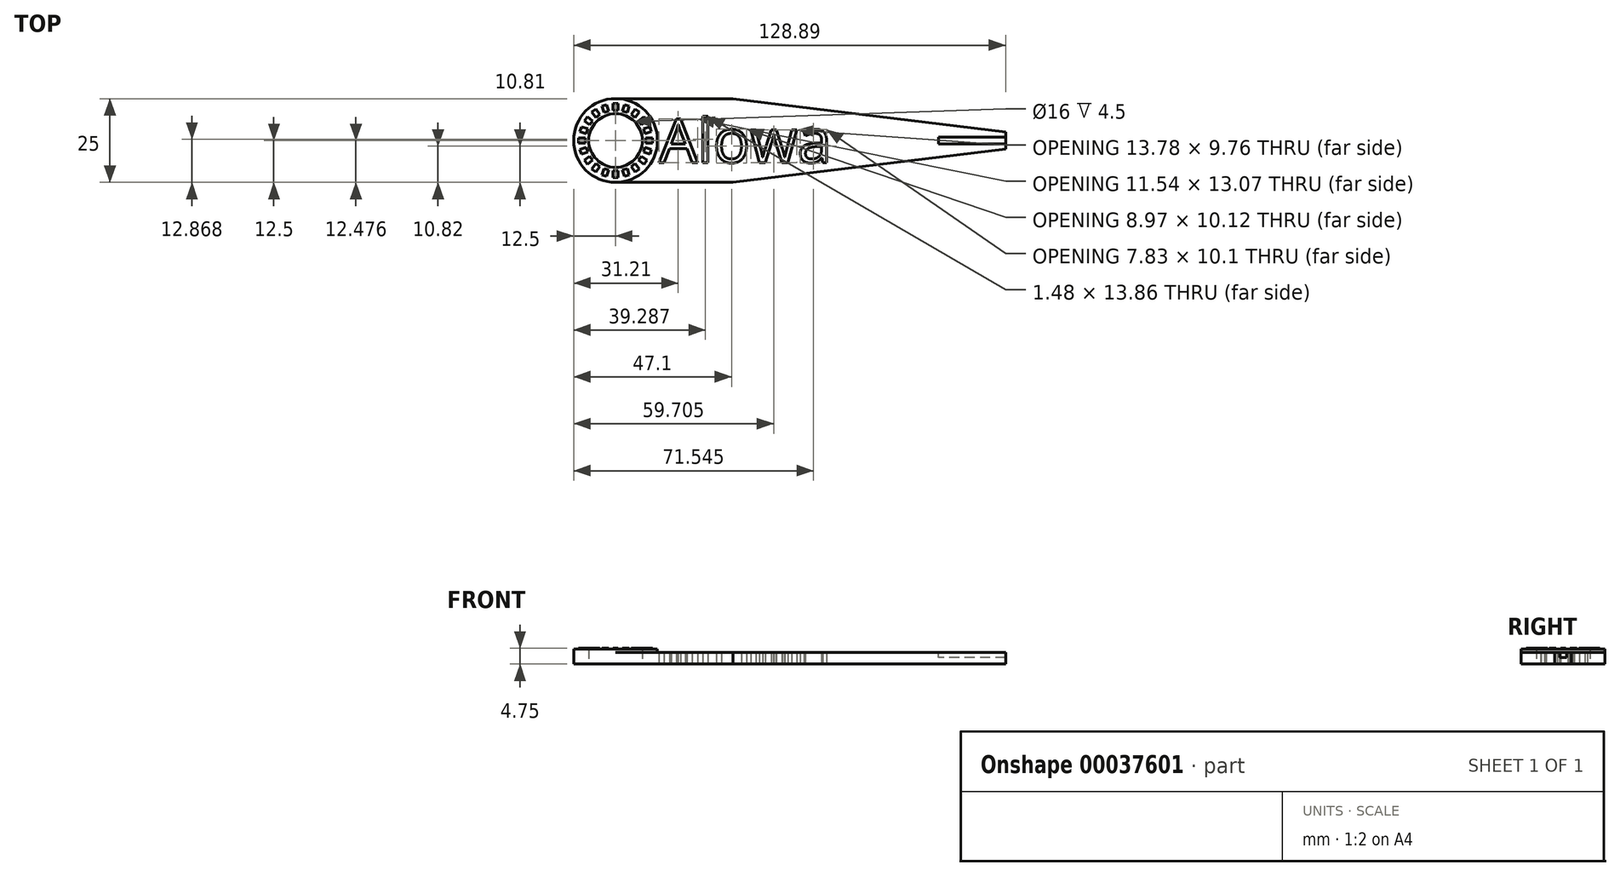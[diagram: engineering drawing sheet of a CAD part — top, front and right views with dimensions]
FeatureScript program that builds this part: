
annotation { "Feature Type Name" : "Feature", "Feature Type Description" : "" }
export const myFeature = defineFeature(function(context is Context, id is Id, definition is map)
    precondition{}
    {
        {
            var Q0;
            Q0=qCreatedBy(makeId("Top.planeOp"),FACE);
            var sketch = newSketch(context, id + "F0", { "sketchPlane" : qUnion([Q0])});
            skCircle(sketch, "E0", {"center": v(0, 0) * mm, "radius": 8 * mm});
            skCircle(sketch, "E1", {"center": v(0, 0) * mm, "radius": 12.5 * mm});
            skLineSegment(sketch, "E2", {"start": v(0, 12.5) * mm, "end": v(35, 12.5) * mm});
            skPoint(sketch, "E3", {"position": v(0, 12.5) * mm});
            skLineSegment(sketch, "E4", {"start": v(0, 0) * mm, "end": v(56.27, 0) * mm, "construction": true});
            skLineSegment(sketch, "E5", {"start": v(35, 12.5) * mm, "end": v(73.46, 12.5) * mm, "construction": true});
            skLineSegment(sketch, "E6", {"start": v(0, -12.5) * mm, "end": v(35, -12.5) * mm});
            skLineSegment(sketch, "E7", {"start": v(35, 12.5) * mm, "end": v(116.39, 2.5) * mm});
            skLineSegment(sketch, "E8.MirrorCS", {"start": v(35, -12.5) * mm, "end": v(116.39, -2.5) * mm});
            skLineSegment(sketch, "E9", {"start": v(116.39, 2.5) * mm, "end": v(116.39, -2.5) * mm});
            skSolve(sketch);
        }
        {
            var Q0;
            Q0 = qSketchRegion(id + "F0", true);
            extrude(context, id + "F1", {"entities" : qUnion([Q0]), "depth" : 3.5 * mm});
        }
        {
            var Q0;
            Q0=makeQuery(id+"F1.opExtrude","CAP_FACE",FACE,{"disambiguationData":[OSD([sQuery(id+"F0.wireOp",EDGE,"E0"),sQuery(id+"F0.wireOp",EDGE,"E1"),sQuery(id+"F0.wireOp",EDGE,"E2"),sQuery(id+"F0.wireOp",EDGE,"E6"),sQuery(id+"F0.wireOp",EDGE,"E7"),sQuery(id+"F0.wireOp",EDGE,"E8.MirrorCS"),sQuery(id+"F0.wireOp",EDGE,"E9")])],"isStart":false});
            var sketch = newSketch(context, id + "F2", { "sketchPlane" : qUnion([Q0])});
            skCircle(sketch, "E10", {"center": v(0, 0) * mm, "radius": 12.5 * mm});
            skCircle(sketch, "E11", {"center": v(0, 0) * mm, "radius": 8 * mm});
            skSolve(sketch);
        }
        {
            var Q0;
            Q0=makeQuery(id+"F2.imprint","IMPRINT",FACE,{"disambiguationData":[TD([[makeQuery(id+"F2.imprint","IMPRINT",EDGE,{"derivedFrom":sQuery(id+"F2.wireOp",EDGE,"E11")}),-1.0]])]});
            extrude(context, id + "F3", {"entities" : qUnion([Q0]), "operationType" : NewBodyOperationType.ADD, "depth" : 1 * mm});
        }
        {
            var Q0;
            Q0=makeQuery(id+"F3.opExtrude","CAP_FACE",FACE,{"disambiguationData":[OSD([sQuery(id+"F2.wireOp",EDGE,"E10"),sQuery(id+"F2.wireOp",EDGE,"E11")])],"isStart":false});
            var sketch = newSketch(context, id + "F4", { "sketchPlane" : qUnion([Q0])});
            skLineSegment(sketch, "E12.bottom", {"start": v(-0.75, 11) * mm, "end": v(0.75, 11) * mm});
            skLineSegment(sketch, "E12.top", {"start": v(-0.75, 9) * mm, "end": v(0.75, 9) * mm});
            skLineSegment(sketch, "E12.left", {"start": v(-0.75, 11) * mm, "end": v(-0.75, 9) * mm});
            skLineSegment(sketch, "E12.right", {"start": v(0.75, 11) * mm, "end": v(0.75, 9) * mm});
            skPoint(sketch, "E13", {"position": v(0, 8) * mm});
            skLineSegment(sketch, "E14.1.0", {"start": v(-4.11, 10.23) * mm, "end": v(-2.69, 10.7) * mm});
            skLineSegment(sketch, "E14.1.1", {"start": v(-4.11, 10.23) * mm, "end": v(-3.5, 8.33) * mm});
            skLineSegment(sketch, "E14.1.2", {"start": v(-3.5, 8.33) * mm, "end": v(-2.07, 8.8) * mm});
            skLineSegment(sketch, "E14.1.3", {"start": v(-2.69, 10.7) * mm, "end": v(-2.07, 8.8) * mm});
            skLineSegment(sketch, "E14.2.0", {"start": v(-7.07, 8.46) * mm, "end": v(-5.86, 9.34) * mm});
            skLineSegment(sketch, "E14.2.1", {"start": v(-7.07, 8.46) * mm, "end": v(-5.9, 6.84) * mm});
            skLineSegment(sketch, "E14.2.2", {"start": v(-5.9, 6.84) * mm, "end": v(-4.68, 7.72) * mm});
            skLineSegment(sketch, "E14.2.3", {"start": v(-5.86, 9.34) * mm, "end": v(-4.68, 7.72) * mm});
            skPoint(sketch, "E14.center", {"position": v(0, 0) * mm});
            skLineSegment(sketch, "E15.1.3.0", {"start": v(-9.34, 5.86) * mm, "end": v(-8.46, 7.07) * mm});
            skLineSegment(sketch, "E15.3.3.0", {"start": v(-9.34, 5.86) * mm, "end": v(-7.72, 4.68) * mm});
            skLineSegment(sketch, "E15.6.3.0", {"start": v(-7.72, 4.68) * mm, "end": v(-6.84, 5.9) * mm});
            skLineSegment(sketch, "E15.9.3.0", {"start": v(-8.46, 7.07) * mm, "end": v(-6.84, 5.9) * mm});
            skLineSegment(sketch, "E15.1.4.0", {"start": v(-10.7, 2.69) * mm, "end": v(-10.23, 4.11) * mm});
            skLineSegment(sketch, "E15.3.4.0", {"start": v(-10.7, 2.69) * mm, "end": v(-8.8, 2.07) * mm});
            skLineSegment(sketch, "E15.6.4.0", {"start": v(-8.8, 2.07) * mm, "end": v(-8.33, 3.5) * mm});
            skLineSegment(sketch, "E15.9.4.0", {"start": v(-10.23, 4.11) * mm, "end": v(-8.33, 3.5) * mm});
            skLineSegment(sketch, "E15.1.5.0", {"start": v(-11, -0.75) * mm, "end": v(-11, 0.75) * mm});
            skLineSegment(sketch, "E15.3.5.0", {"start": v(-11, -0.75) * mm, "end": v(-9, -0.75) * mm});
            skLineSegment(sketch, "E15.6.5.0", {"start": v(-9, -0.75) * mm, "end": v(-9, 0.75) * mm});
            skLineSegment(sketch, "E15.9.5.0", {"start": v(-11, 0.75) * mm, "end": v(-9, 0.75) * mm});
            skLineSegment(sketch, "E15.1.6.0", {"start": v(-10.23, -4.11) * mm, "end": v(-10.7, -2.69) * mm});
            skLineSegment(sketch, "E15.3.6.0", {"start": v(-10.23, -4.11) * mm, "end": v(-8.33, -3.5) * mm});
            skLineSegment(sketch, "E15.6.6.0", {"start": v(-8.33, -3.5) * mm, "end": v(-8.8, -2.07) * mm});
            skLineSegment(sketch, "E15.9.6.0", {"start": v(-10.7, -2.69) * mm, "end": v(-8.8, -2.07) * mm});
            skLineSegment(sketch, "E15.1.7.0", {"start": v(-8.46, -7.07) * mm, "end": v(-9.34, -5.86) * mm});
            skLineSegment(sketch, "E15.3.7.0", {"start": v(-8.46, -7.07) * mm, "end": v(-6.84, -5.9) * mm});
            skLineSegment(sketch, "E15.6.7.0", {"start": v(-6.84, -5.9) * mm, "end": v(-7.72, -4.68) * mm});
            skLineSegment(sketch, "E15.9.7.0", {"start": v(-9.34, -5.86) * mm, "end": v(-7.72, -4.68) * mm});
            skLineSegment(sketch, "E15.1.8.0", {"start": v(-5.86, -9.34) * mm, "end": v(-7.07, -8.46) * mm});
            skLineSegment(sketch, "E15.3.8.0", {"start": v(-5.86, -9.34) * mm, "end": v(-4.68, -7.72) * mm});
            skLineSegment(sketch, "E15.6.8.0", {"start": v(-4.68, -7.72) * mm, "end": v(-5.9, -6.84) * mm});
            skLineSegment(sketch, "E15.9.8.0", {"start": v(-7.07, -8.46) * mm, "end": v(-5.9, -6.84) * mm});
            skLineSegment(sketch, "E15.1.9.0", {"start": v(-2.69, -10.7) * mm, "end": v(-4.11, -10.23) * mm});
            skLineSegment(sketch, "E15.3.9.0", {"start": v(-2.69, -10.7) * mm, "end": v(-2.07, -8.8) * mm});
            skLineSegment(sketch, "E15.6.9.0", {"start": v(-2.07, -8.8) * mm, "end": v(-3.5, -8.33) * mm});
            skLineSegment(sketch, "E15.9.9.0", {"start": v(-4.11, -10.23) * mm, "end": v(-3.5, -8.33) * mm});
            skLineSegment(sketch, "E15.1.10.0", {"start": v(0.75, -11) * mm, "end": v(-0.75, -11) * mm});
            skLineSegment(sketch, "E15.3.10.0", {"start": v(0.75, -11) * mm, "end": v(0.75, -9) * mm});
            skLineSegment(sketch, "E15.6.10.0", {"start": v(0.75, -9) * mm, "end": v(-0.75, -9) * mm});
            skLineSegment(sketch, "E15.9.10.0", {"start": v(-0.75, -11) * mm, "end": v(-0.75, -9) * mm});
            skLineSegment(sketch, "E15.1.11.0", {"start": v(4.11, -10.23) * mm, "end": v(2.69, -10.7) * mm});
            skLineSegment(sketch, "E15.3.11.0", {"start": v(4.11, -10.23) * mm, "end": v(3.5, -8.33) * mm});
            skLineSegment(sketch, "E15.6.11.0", {"start": v(3.5, -8.33) * mm, "end": v(2.07, -8.8) * mm});
            skLineSegment(sketch, "E15.9.11.0", {"start": v(2.69, -10.7) * mm, "end": v(2.07, -8.8) * mm});
            skLineSegment(sketch, "E15.1.12.0", {"start": v(7.07, -8.46) * mm, "end": v(5.86, -9.34) * mm});
            skLineSegment(sketch, "E15.3.12.0", {"start": v(7.07, -8.46) * mm, "end": v(5.9, -6.84) * mm});
            skLineSegment(sketch, "E15.6.12.0", {"start": v(5.9, -6.84) * mm, "end": v(4.68, -7.72) * mm});
            skLineSegment(sketch, "E15.9.12.0", {"start": v(5.86, -9.34) * mm, "end": v(4.68, -7.72) * mm});
            skLineSegment(sketch, "E15.1.13.0", {"start": v(9.34, -5.86) * mm, "end": v(8.46, -7.07) * mm});
            skLineSegment(sketch, "E15.3.13.0", {"start": v(9.34, -5.86) * mm, "end": v(7.72, -4.68) * mm});
            skLineSegment(sketch, "E15.6.13.0", {"start": v(7.72, -4.68) * mm, "end": v(6.84, -5.9) * mm});
            skLineSegment(sketch, "E15.9.13.0", {"start": v(8.46, -7.07) * mm, "end": v(6.84, -5.9) * mm});
            skLineSegment(sketch, "E15.1.14.0", {"start": v(10.7, -2.69) * mm, "end": v(10.23, -4.11) * mm});
            skLineSegment(sketch, "E15.3.14.0", {"start": v(10.7, -2.69) * mm, "end": v(8.8, -2.07) * mm});
            skLineSegment(sketch, "E15.6.14.0", {"start": v(8.8, -2.07) * mm, "end": v(8.33, -3.5) * mm});
            skLineSegment(sketch, "E15.9.14.0", {"start": v(10.23, -4.11) * mm, "end": v(8.33, -3.5) * mm});
            skLineSegment(sketch, "E15.1.15.0", {"start": v(11, 0.75) * mm, "end": v(11, -0.75) * mm});
            skLineSegment(sketch, "E15.3.15.0", {"start": v(11, 0.75) * mm, "end": v(9, 0.75) * mm});
            skLineSegment(sketch, "E15.6.15.0", {"start": v(9, 0.75) * mm, "end": v(9, -0.75) * mm});
            skLineSegment(sketch, "E15.9.15.0", {"start": v(11, -0.75) * mm, "end": v(9, -0.75) * mm});
            skLineSegment(sketch, "E15.1.16.0", {"start": v(10.23, 4.11) * mm, "end": v(10.7, 2.69) * mm});
            skLineSegment(sketch, "E15.3.16.0", {"start": v(10.23, 4.11) * mm, "end": v(8.33, 3.5) * mm});
            skLineSegment(sketch, "E15.6.16.0", {"start": v(8.33, 3.5) * mm, "end": v(8.8, 2.07) * mm});
            skLineSegment(sketch, "E15.9.16.0", {"start": v(10.7, 2.69) * mm, "end": v(8.8, 2.07) * mm});
            skLineSegment(sketch, "E15.1.17.0", {"start": v(8.46, 7.07) * mm, "end": v(9.34, 5.86) * mm});
            skLineSegment(sketch, "E15.3.17.0", {"start": v(8.46, 7.07) * mm, "end": v(6.84, 5.9) * mm});
            skLineSegment(sketch, "E15.6.17.0", {"start": v(6.84, 5.9) * mm, "end": v(7.72, 4.68) * mm});
            skLineSegment(sketch, "E15.9.17.0", {"start": v(9.34, 5.86) * mm, "end": v(7.72, 4.68) * mm});
            skLineSegment(sketch, "E15.1.18.0", {"start": v(5.86, 9.34) * mm, "end": v(7.07, 8.46) * mm});
            skLineSegment(sketch, "E15.3.18.0", {"start": v(5.86, 9.34) * mm, "end": v(4.68, 7.72) * mm});
            skLineSegment(sketch, "E15.6.18.0", {"start": v(4.68, 7.72) * mm, "end": v(5.9, 6.84) * mm});
            skLineSegment(sketch, "E15.9.18.0", {"start": v(7.07, 8.46) * mm, "end": v(5.9, 6.84) * mm});
            skLineSegment(sketch, "E15.1.19.0", {"start": v(2.69, 10.7) * mm, "end": v(4.11, 10.23) * mm});
            skLineSegment(sketch, "E15.3.19.0", {"start": v(2.69, 10.7) * mm, "end": v(2.07, 8.8) * mm});
            skLineSegment(sketch, "E15.6.19.0", {"start": v(2.07, 8.8) * mm, "end": v(3.5, 8.33) * mm});
            skLineSegment(sketch, "E15.9.19.0", {"start": v(4.11, 10.23) * mm, "end": v(3.5, 8.33) * mm});
            skSolve(sketch);
        }
        {
            var Q0;
            Q0 = qSketchRegion(id + "F4", true);
            extrude(context, id + "F5", {"entities" : qUnion([Q0]), "operationType" : NewBodyOperationType.ADD, "depth" : .25 * mm});
        }
        {
            var Q0;
            Q0=makeQuery(id+"F1.opExtrude","CAP_FACE",FACE,{"disambiguationData":[OSD([sQuery(id+"F0.wireOp",EDGE,"E0"),sQuery(id+"F0.wireOp",EDGE,"E1"),sQuery(id+"F0.wireOp",EDGE,"E2"),sQuery(id+"F0.wireOp",EDGE,"E6"),sQuery(id+"F0.wireOp",EDGE,"E7"),sQuery(id+"F0.wireOp",EDGE,"E8.MirrorCS"),sQuery(id+"F0.wireOp",EDGE,"E9")])],"isStart":false});
            var sketch = newSketch(context, id + "F6", { "sketchPlane" : qUnion([Q0])});
            skLineSegment(sketch, "E16.bottom", {"start": v(116.39, 1) * mm, "end": v(96.39, 1) * mm});
            skLineSegment(sketch, "E16.top", {"start": v(116.39, -1) * mm, "end": v(96.39, -1) * mm});
            skLineSegment(sketch, "E16.left", {"start": v(116.39, 1) * mm, "end": v(116.39, -1) * mm});
            skLineSegment(sketch, "E16.right", {"start": v(96.39, 1) * mm, "end": v(96.39, -1) * mm});
            skSolve(sketch);
        }
        {
            var Q0;
            Q0 = qSketchRegion(id + "F6", true);
            extrude(context, id + "F7", {"entities" : qUnion([Q0]), "operationType" : NewBodyOperationType.REMOVE, "oppositeDirection" : true, "depth" : 1.5 * mm});
        }
        {
            var Q0;
            Q0=qCreatedBy(makeId("Top.planeOp"),FACE);
            var sketch = newSketch(context, id + "F8", { "sketchPlane" : qUnion([Q0])});
            skText(sketch, "E17", { "text": "Alowa", "fontName": "OpenSans-Regular.ttf"});
            const initialGuessF8  = {"E17": [0.01294, -0.00656, 1, 0, 0.01313]};
            skSetInitialGuess(sketch, initialGuessF8);
            skSolve(sketch);
        }
        {
            var Q0;
            Q0 = qSketchRegion(id + "F8", true);
            extrude(context, id + "F9", {"entities" : qUnion([Q0]), "operationType" : NewBodyOperationType.REMOVE, "depth" : 25 * mm});
        }
    });
